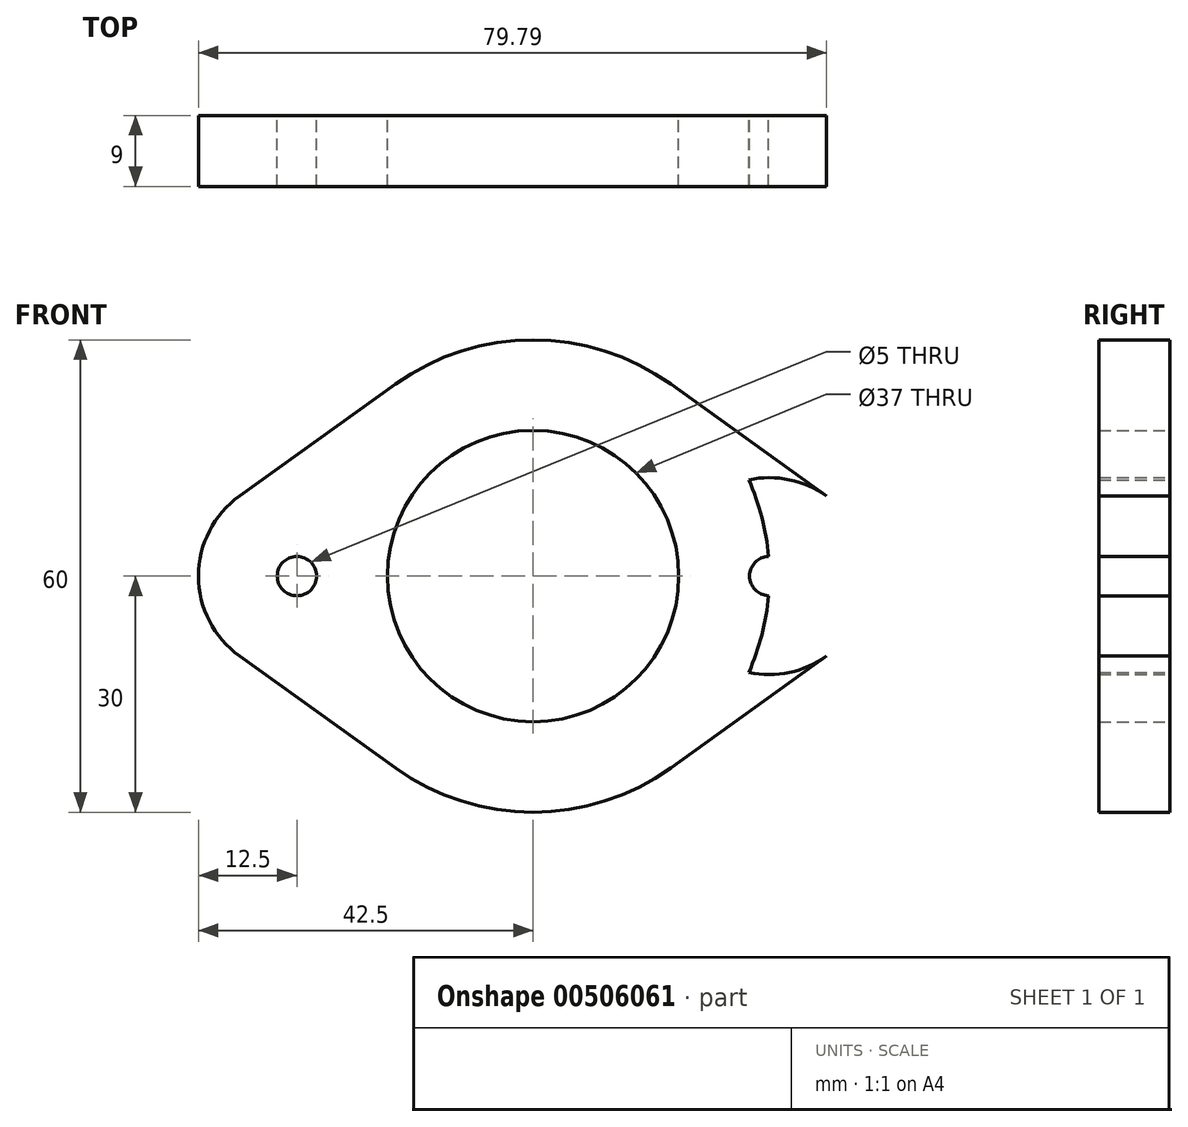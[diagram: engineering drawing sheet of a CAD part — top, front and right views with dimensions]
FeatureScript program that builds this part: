
annotation { "Feature Type Name" : "Feature", "Feature Type Description" : "" }
export const myFeature = defineFeature(function(context is Context, id is Id, definition is map)
    precondition{}
    {
        {
            var Q0;
            Q0=qCreatedBy(makeId("Front.planeOp"),FACE);
            var sketch = newSketch(context, id + "F0", { "sketchPlane" : qUnion([Q0])});
            skCircle(sketch, "E0", {"center": v(0, 0) * mm, "radius": 18.5 * mm});
            skLineSegment(sketch, "E1", {"start": v(-30, 0) * mm, "end": v(30, 0) * mm, "construction": true});
            skCircle(sketch, "E2", {"center": v(-30, 0) * mm, "radius": 2.5 * mm});
            skCircle(sketch, "E3", {"center": v(30, 0) * mm, "radius": 2.5 * mm});
            skCircle(sketch, "E4", {"center": v(0, 0) * mm, "radius": 30 * mm});
            skCircle(sketch, "E5", {"center": v(30, 0) * mm, "radius": 12.5 * mm});
            skCircle(sketch, "E6", {"center": v(-30, 0) * mm, "radius": 12.5 * mm});
            skLineSegment(sketch, "E7", {"start": v(-17.5, 24.37) * mm, "end": v(-37.3, 10.15) * mm});
            skLineSegment(sketch, "E8", {"start": v(-37.3, -10.15) * mm, "end": v(-17.5, -24.37) * mm});
            skLineSegment(sketch, "E9", {"start": v(17.5, -24.37) * mm, "end": v(37.3, -10.15) * mm});
            skLineSegment(sketch, "E10", {"start": v(17.5, 24.37) * mm, "end": v(37.3, 10.15) * mm});
            skSolve(sketch);
        }
        {
            var Q0;
            {var subQ0=sQuery(id+"F0.wireOp",EDGE,"E9");Q0=makeQuery(id+"F0.imprint","IMPRINT",FACE,{"disambiguationData":[TD([[makeQuery(id+"F0.imprint","IMPRINT",EDGE,{"derivedFrom":subQ0}),1.0]])]});}
            var Q1;
            {var subQ2=sQuery(id+"F0.wireOp",EDGE,"E4");var subQ4=sQuery(id+"F0.wireOp",EDGE,"E2");var subQ5=makeQuery(id+"F0.imprint","INTERSECT",VERTEX,{"disambiguationData":[OD(0.0)],"derivedFrom":[subQ4,subQ2]});Q1=makeQuery(id+"F0.imprint","IMPRINT",FACE,{"disambiguationData":[TD([[makeQuery(id+"F0.imprint","IMPRINT",EDGE,{"disambiguationData":[TD([[subQ5,-1.0]])],"derivedFrom":subQ4}),-1.0]])]});}
            var Q2;
            {var subQ3=sQuery(id+"F0.wireOp",EDGE,"E6");var subQ7=sQuery(id+"F0.wireOp",EDGE,"E0");var subQ8=makeQuery(id+"F0.imprint","INTERSECT",VERTEX,{"disambiguationData":[OD(1.0)],"derivedFrom":[subQ7,subQ3]});Q2=makeQuery(id+"F0.imprint","IMPRINT",FACE,{"disambiguationData":[TD([[makeQuery(id+"F0.imprint","IMPRINT",EDGE,{"disambiguationData":[TD([[subQ8,-1.0]])],"derivedFrom":subQ7}),-1.0]])]});}
            var Q3;
            {var subQ4=sQuery(id+"F0.wireOp",EDGE,"E5");var subQ7=sQuery(id+"F0.wireOp",EDGE,"E0");var subQ8=makeQuery(id+"F0.imprint","INTERSECT",VERTEX,{"disambiguationData":[OD(0.0)],"derivedFrom":[subQ7,subQ4]});Q3=makeQuery(id+"F0.imprint","IMPRINT",FACE,{"disambiguationData":[TD([[makeQuery(id+"F0.imprint","IMPRINT",EDGE,{"disambiguationData":[TD([[subQ8,1.0]])],"derivedFrom":subQ7}),-1.0]])]});}
            var Q4;
            {var subQ0=sQuery(id+"F0.wireOp",EDGE,"E10");Q4=makeQuery(id+"F0.imprint","IMPRINT",FACE,{"disambiguationData":[TD([[makeQuery(id+"F0.imprint","IMPRINT",EDGE,{"derivedFrom":subQ0}),-1.0]])]});}
            var Q5;
            {var subQ0=sQuery(id+"F0.wireOp",EDGE,"E7");Q5=makeQuery(id+"F0.imprint","IMPRINT",FACE,{"disambiguationData":[TD([[makeQuery(id+"F0.imprint","IMPRINT",EDGE,{"derivedFrom":subQ0}),1.0]])]});}
            var Q6;
            {var subQ2=sQuery(id+"F0.wireOp",EDGE,"E4");var subQ4=sQuery(id+"F0.wireOp",EDGE,"E3");var subQ7=makeQuery(id+"F0.imprint","INTERSECT",VERTEX,{"disambiguationData":[OD(0.0)],"derivedFrom":[subQ4,subQ2]});Q6=makeQuery(id+"F0.imprint","IMPRINT",FACE,{"disambiguationData":[TD([[makeQuery(id+"F0.imprint","IMPRINT",EDGE,{"disambiguationData":[TD([[subQ7,1.0]])],"derivedFrom":subQ4}),-1.0]])]});}
            var Q7;
            {var subQ0=sQuery(id+"F0.wireOp",EDGE,"E8");Q7=makeQuery(id+"F0.imprint","IMPRINT",FACE,{"disambiguationData":[TD([[makeQuery(id+"F0.imprint","IMPRINT",EDGE,{"derivedFrom":subQ0}),1.0]])]});}
            var Q8;
            {var subQ3=sQuery(id+"F0.wireOp",EDGE,"E6");var subQ7=sQuery(id+"F0.wireOp",EDGE,"E0");var subQ8=makeQuery(id+"F0.imprint","INTERSECT",VERTEX,{"disambiguationData":[OD(0.0)],"derivedFrom":[subQ7,subQ3]});Q8=makeQuery(id+"F0.imprint","IMPRINT",FACE,{"disambiguationData":[TD([[makeQuery(id+"F0.imprint","IMPRINT",EDGE,{"disambiguationData":[TD([[subQ8,-1.0]])],"derivedFrom":subQ7}),-1.0]])]});}
            var Q9;
            {var subQ2=sQuery(id+"F0.wireOp",EDGE,"E6");var subQ4=sQuery(id+"F0.wireOp",EDGE,"E0");var subQ5=makeQuery(id+"F0.imprint","INTERSECT",VERTEX,{"disambiguationData":[OD(0.0)],"derivedFrom":[subQ4,subQ2]});Q9=makeQuery(id+"F0.imprint","IMPRINT",FACE,{"disambiguationData":[TD([[makeQuery(id+"F0.imprint","IMPRINT",EDGE,{"disambiguationData":[TD([[subQ5,1.0]])],"derivedFrom":subQ4}),-1.0]])]});}
            extrude(context, id + "F1", {"entities" : qUnion([Q0, Q1, Q2, Q3, Q4, Q5, Q6, Q7, Q8, Q9]), "depth" : 9 * mm});
        }
    });
